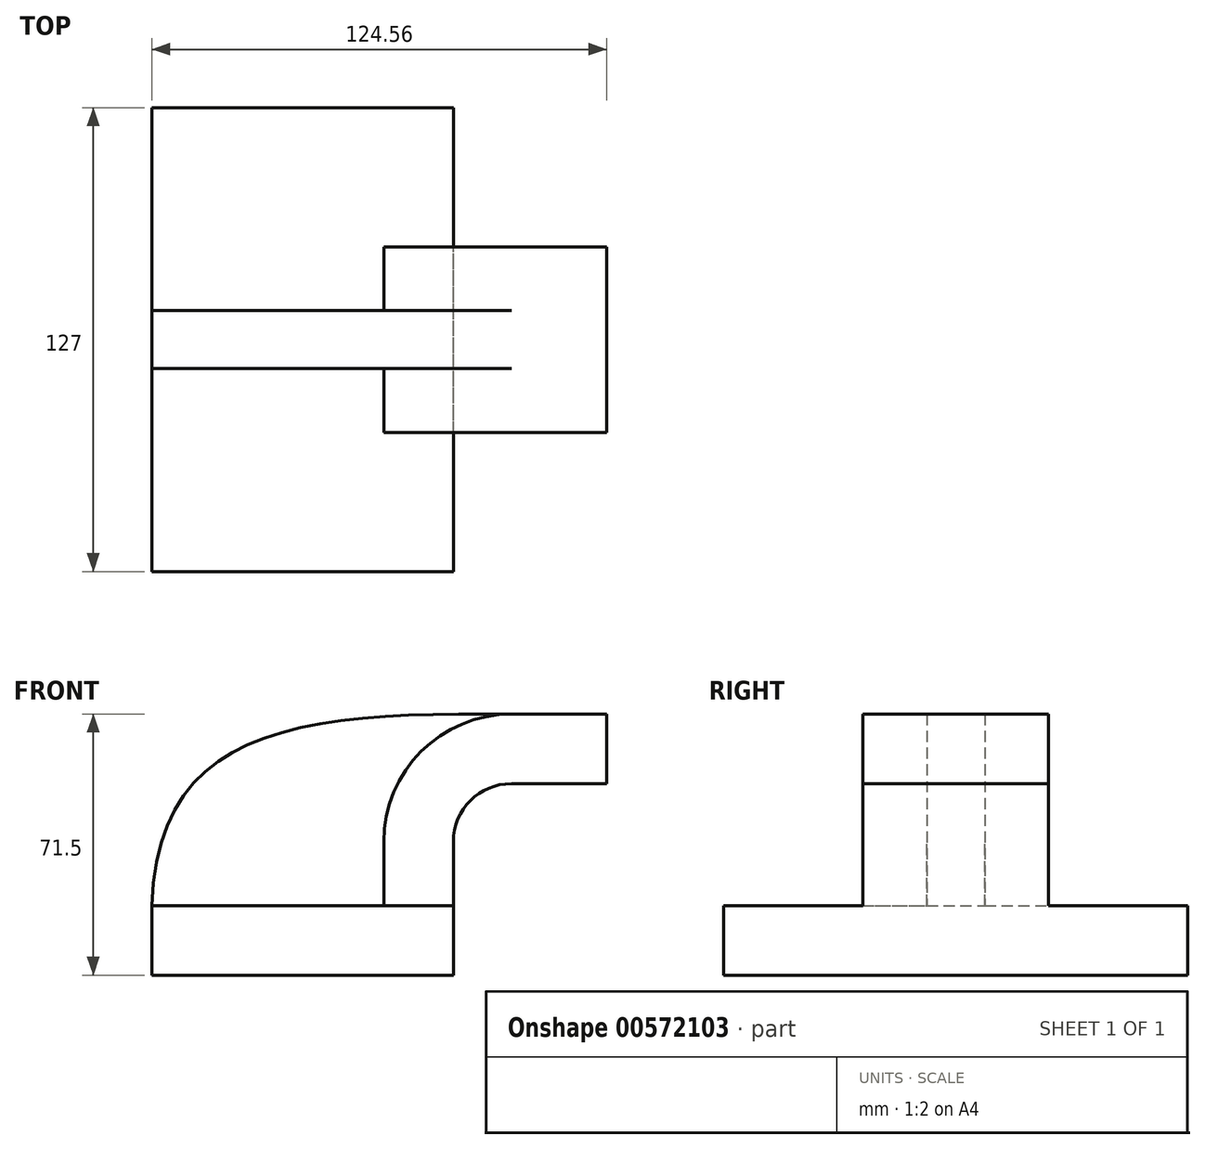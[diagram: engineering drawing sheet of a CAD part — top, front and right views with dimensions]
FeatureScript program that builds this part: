
annotation { "Feature Type Name" : "Feature", "Feature Type Description" : "" }
export const myFeature = defineFeature(function(context is Context, id is Id, definition is map)
    precondition{}
    {
        {
            var Q0;
            Q0=qCreatedBy(makeId("Front.planeOp"),FACE);
            var sketch = newSketch(context, id + "F0", { "sketchPlane" : qUnion([Q0])});
            skLineSegment(sketch, "E0.bottom", {"start": v(-41.28, 9.52) * mm, "end": v(41.28, 9.52) * mm});
            skLineSegment(sketch, "E0.top", {"start": v(-41.28, -9.53) * mm, "end": v(41.28, -9.53) * mm});
            skLineSegment(sketch, "E0.left", {"start": v(-41.28, 9.52) * mm, "end": v(-41.28, -9.53) * mm});
            skLineSegment(sketch, "E0.right", {"start": v(41.28, 9.52) * mm, "end": v(41.28, -9.53) * mm});
            skPoint(sketch, "E0.middle", {"position": v(0, 0) * mm});
            skLineSegment(sketch, "E1.bottom", {"start": v(60.33, 66.67) * mm, "end": v(111.12, 66.67) * mm});
            skLineSegment(sketch, "E1.top", {"start": v(60.33, 38.1) * mm, "end": v(111.13, 38.1) * mm});
            skLineSegment(sketch, "E1.left", {"start": v(60.33, 66.67) * mm, "end": v(60.33, 38.1) * mm});
            skLineSegment(sketch, "E1.right", {"start": v(111.13, 66.67) * mm, "end": v(111.13, 38.1) * mm});
            skPoint(sketch, "E1.middle", {"position": v(85.73, 52.39) * mm});
            skLineSegment(sketch, "E2", {"start": v(41.28, 9.52) * mm, "end": v(41.28, 27) * mm});
            skArc(sketch, "E3", {"start": v(57.15, 42.88) * mm, "mid": v(45.92, 38.23) * mm, "end": v(41.28, 27) * mm});
            skLineSegment(sketch, "E4", {"start": v(41.28, -9.53) * mm, "end": v(114.36, -9.53) * mm});
            skLineSegment(sketch, "E5", {"start": v(57.15, 42.88) * mm, "end": v(83.3, 42.88) * mm});
            skLineSegment(sketch, "E6.0", {"start": v(57.15, 61.93) * mm, "end": v(83.3, 61.93) * mm});
            skArc(sketch, "E6.1", {"start": v(57.15, 61.93) * mm, "mid": v(32.45, 51.7) * mm, "end": v(22.23, 27) * mm});
            skLineSegment(sketch, "E6.2", {"start": v(22.23, 9.52) * mm, "end": v(22.23, 27) * mm});
            skLineSegment(sketch, "E7", {"start": v(83.21, 66.67) * mm, "end": v(83.3, 38.1) * mm});
            skFitSpline(sketch, "E8", {"points": [v(57.15, 61.93) * mm, v(-41.28, 9.52) * mm], "startDerivative": vector(-171.45, 1.6) * mm, "endDerivative": vector(-5.28, -148.35) * mm});
            skSolve(sketch);
        }
        {
            var Q0;
            Q0=makeQuery(id+"F0.imprint","IMPRINT",FACE,{"disambiguationData":[TD([[makeQuery(id+"F0.imprint","IMPRINT",EDGE,{"derivedFrom":sQuery(id+"F0.wireOp",EDGE,"E0.top")}),1.0]])]});
            extrude(context, id + "F1", {"entities" : qUnion([Q0]), "endBound" : BoundingType.SYMMETRIC, "depth" : 127 * mm, "offsetDistance" : 25.4 * mm});
        }
        {
            var Q0;
            {var subQ1=sQuery(id+"F0.wireOp",EDGE,"E2");Q0=makeQuery(id+"F0.imprint","IMPRINT",FACE,{"disambiguationData":[TD([[makeQuery(id+"F0.imprint","IMPRINT",EDGE,{"derivedFrom":subQ1}),1.0]])]});}
            var Q1;
            {var subQ0=sQuery(id+"F0.wireOp",EDGE,"E6.0");var subQ1=sQuery(id+"F0.wireOp",EDGE,"E1.left");var subQ2=makeQuery(id+"F0.imprint","INTERSECT",VERTEX,{"derivedFrom":[subQ1,subQ0]});Q1=makeQuery(id+"F0.imprint","IMPRINT",FACE,{"disambiguationData":[TD([[makeQuery(id+"F0.imprint","IMPRINT",EDGE,{"disambiguationData":[TD([[subQ2,-1.0]])],"derivedFrom":subQ1}),1.0]])]});}
            extrude(context, id + "F2", {"entities" : qUnion([Q0, Q1]), "operationType" : NewBodyOperationType.ADD, "endBound" : BoundingType.SYMMETRIC, "depth" : 50.8 * mm, "offsetDistance" : 25.4 * mm});
        }
        {
            var Q0;
            Q0=makeQuery(id+"F0.imprint","IMPRINT",FACE,{"disambiguationData":[TD([[makeQuery(id+"F0.imprint","IMPRINT",EDGE,{"derivedFrom":sQuery(id+"F0.wireOp",EDGE,"E6.1")}),-1.0]])]});
            extrude(context, id + "F3", {"entities" : qUnion([Q0]), "operationType" : NewBodyOperationType.ADD, "endBound" : BoundingType.SYMMETRIC, "depth" : 15.88 * mm, "offsetDistance" : 25.4 * mm});
        }
    });
